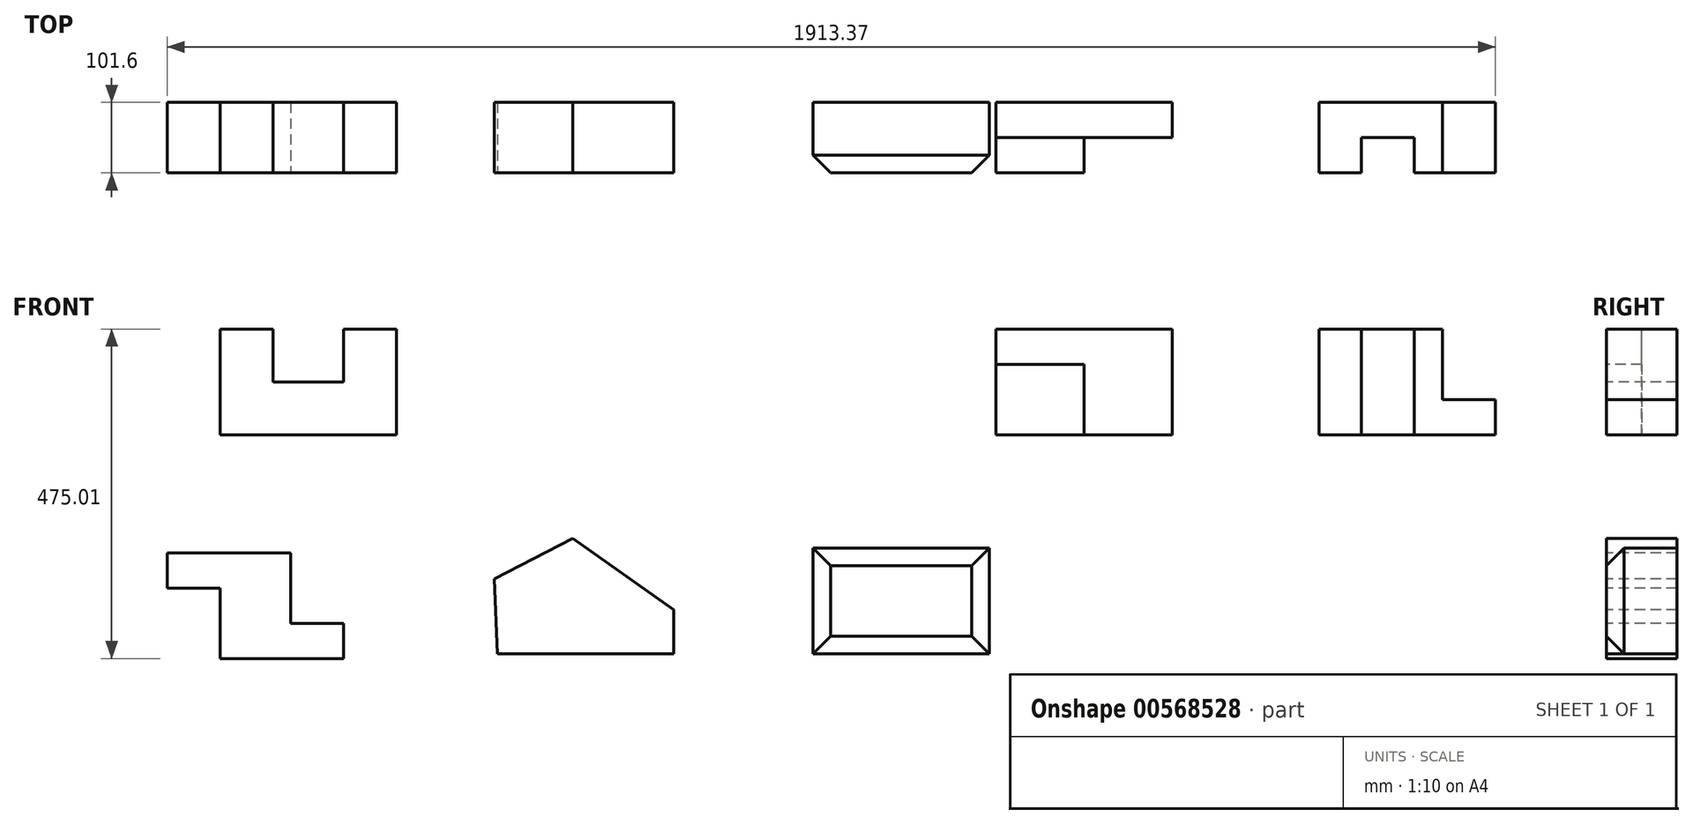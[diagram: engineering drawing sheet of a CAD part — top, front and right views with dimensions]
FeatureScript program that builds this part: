
annotation { "Feature Type Name" : "Feature", "Feature Type Description" : "" }
export const myFeature = defineFeature(function(context is Context, id is Id, definition is map)
    precondition{}
    {
        {
            var Q0;
            Q0=qCreatedBy(makeId("Front.planeOp"),FACE);
            var sketch = newSketch(context, id + "F0", { "sketchPlane" : qUnion([Q0])});
            skLineSegment(sketch, "E0", {"start": v(0, 0) * mm, "end": v(254, 0) * mm});
            skLineSegment(sketch, "E1", {"start": v(254, 0) * mm, "end": v(254, 152.4) * mm});
            skLineSegment(sketch, "E2", {"start": v(254, 152.4) * mm, "end": v(177.8, 152.4) * mm});
            skLineSegment(sketch, "E3", {"start": v(177.8, 152.4) * mm, "end": v(177.8, 76.2) * mm});
            skLineSegment(sketch, "E4", {"start": v(177.8, 76.2) * mm, "end": v(76.2, 76.2) * mm});
            skLineSegment(sketch, "E5", {"start": v(76.2, 76.2) * mm, "end": v(76.2, 152.4) * mm});
            skLineSegment(sketch, "E6", {"start": v(76.2, 152.4) * mm, "end": v(0, 152.4) * mm});
            skLineSegment(sketch, "E7", {"start": v(0, 152.4) * mm, "end": v(0, 0) * mm});
            skSolve(sketch);
        }
        {
            var Q0;
            Q0=makeQuery(id+"F0.imprint","IMPRINT",FACE,{"disambiguationData":[TD([[makeQuery(id+"F0.imprint","IMPRINT",EDGE,{"derivedFrom":sQuery(id+"F0.wireOp",EDGE,"E0")}),1.0]])]});
            extrude(context, id + "F1", {"entities" : qUnion([Q0]), "oppositeDirection" : true, "depth" : 101.6 * mm, "offsetDistance" : 25.4 * mm});
        }
        {
            var Q0;
            Q0=qCreatedBy(makeId("Front.planeOp"),FACE);
            var sketch = newSketch(context, id + "F2", { "sketchPlane" : qUnion([Q0])});
            skLineSegment(sketch, "E8.bottom", {"start": v(1117.43, 0) * mm, "end": v(1371.43, 0) * mm});
            skLineSegment(sketch, "E8.top", {"start": v(1117.43, 152.4) * mm, "end": v(1371.43, 152.4) * mm});
            skLineSegment(sketch, "E8.left", {"start": v(1117.43, 0) * mm, "end": v(1117.43, 152.4) * mm});
            skLineSegment(sketch, "E8.right", {"start": v(1371.43, 0) * mm, "end": v(1371.43, 152.4) * mm});
            skSolve(sketch);
        }
        {
            var Q0;
            Q0=makeQuery(id+"F2.imprint","IMPRINT",FACE,{"disambiguationData":[TD([[makeQuery(id+"F2.imprint","IMPRINT",EDGE,{"derivedFrom":sQuery(id+"F2.wireOp",EDGE,"E8.bottom")}),1.0]])]});
            extrude(context, id + "F3", {"entities" : qUnion([Q0]), "oppositeDirection" : true, "depth" : 101.6 * mm, "offsetDistance" : 25.4 * mm});
        }
        {
            var Q0;
            Q0=makeQuery(id+"F3.opExtrude","CAP_FACE",FACE,{"disambiguationData":[OSD([sQuery(id+"F2.wireOp",EDGE,"E8.bottom"),sQuery(id+"F2.wireOp",EDGE,"E8.top"),sQuery(id+"F2.wireOp",EDGE,"E8.left"),sQuery(id+"F2.wireOp",EDGE,"E8.right")])],"isStart":true});
            var sketch = newSketch(context, id + "F4", { "sketchPlane" : qUnion([Q0])});
            skLineSegment(sketch, "E9", {"start": v(1117.43, 76.2) * mm, "end": v(1244.43, 76.2) * mm});
            skLineSegment(sketch, "E10", {"start": v(1244.43, 0) * mm, "end": v(1371.43, 0) * mm});
            skLineSegment(sketch, "E11", {"start": v(1371.43, 0) * mm, "end": v(1371.43, 152.4) * mm});
            skLineSegment(sketch, "E12", {"start": v(1371.43, 152.4) * mm, "end": v(1117.43, 152.4) * mm});
            skLineSegment(sketch, "E13", {"start": v(1117.43, 152.4) * mm, "end": v(1117.43, 76.2) * mm});
            skLineSegment(sketch, "E14", {"start": v(1244.43, 76.2) * mm, "end": v(1244.43, 0) * mm});
            skSolve(sketch);
        }
        {
            var Q0;
            {var subQ0=sQuery(id+"F4.wireOp",EDGE,"E9");Q0=makeQuery(id+"F4.imprint","IMPRINT",FACE,{"disambiguationData":[TD([[makeQuery(id+"F4.imprint","IMPRINT",EDGE,{"derivedFrom":subQ0}),-1.0]])]});}
            extrude(context, id + "F5", {"entities" : qUnion([Q0]), "operationType" : NewBodyOperationType.ADD, "depth" : 50.8 * mm, "offsetDistance" : 25.4 * mm});
        }
        {
            var Q0;
            Q0=makeQuery(id+"F5.opExtrude","CAP_FACE",FACE,{"disambiguationData":[OSD([sQuery(id+"F2.wireOp",EDGE,"E8.bottom"),sQuery(id+"F2.wireOp",EDGE,"E8.left"),sQuery(id+"F4.wireOp",EDGE,"E9"),sQuery(id+"F4.wireOp",EDGE,"E14")])],"isStart":false});
            extrude(context, id + "F6", {"entities" : qUnion([Q0]), "operationType" : NewBodyOperationType.ADD, "oppositeDirection" : true, "depth" : 50.8 * mm, "offsetDistance" : 25.4 * mm});
        }
        {
            var Q0;
            Q0=makeQuery(id+"F5.opExtrude","CAP_FACE",FACE,{"disambiguationData":[OSD([sQuery(id+"F2.wireOp",EDGE,"E8.bottom"),sQuery(id+"F2.wireOp",EDGE,"E8.left"),sQuery(id+"F4.wireOp",EDGE,"E9"),sQuery(id+"F4.wireOp",EDGE,"E14")])],"isStart":false});
            extrude(context, id + "F7", {"entities" : qUnion([Q0]), "operationType" : NewBodyOperationType.ADD, "oppositeDirection" : true, "depth" : 50.8 * mm, "offsetDistance" : 25.4 * mm});
        }
        {
            var Q0;
            Q0=makeQuery(id+"F5.opExtrude","CAP_FACE",FACE,{"disambiguationData":[OSD([sQuery(id+"F2.wireOp",EDGE,"E8.bottom"),sQuery(id+"F2.wireOp",EDGE,"E8.left"),sQuery(id+"F4.wireOp",EDGE,"E9"),sQuery(id+"F4.wireOp",EDGE,"E14")])],"isStart":false});
            extrude(context, id + "F8", {"entities" : qUnion([Q0]), "operationType" : NewBodyOperationType.REMOVE, "oppositeDirection" : true, "depth" : 50.8 * mm, "offsetDistance" : 25.4 * mm});
        }
        {
            var Q0;
            {var subQ0=sQuery(id+"F2.wireOp",EDGE,"E8.left");var subQ1=sQuery(id+"F2.wireOp",EDGE,"E8.bottom");Q0=makeQuery(id+"F8.boolean.opBoolean","MERGE",FACE,{"derivedFrom":[makeQuery(id+"F3.opExtrude","CAP_FACE",FACE,{"disambiguationData":[OSD([subQ1,sQuery(id+"F2.wireOp",EDGE,"E8.top"),subQ0,sQuery(id+"F2.wireOp",EDGE,"E8.right")])],"isStart":true}),makeQuery(id+"F8.opExtrude","CAP_FACE",FACE,{"disambiguationData":[OSD([subQ1,subQ0,sQuery(id+"F4.wireOp",EDGE,"E9"),sQuery(id+"F4.wireOp",EDGE,"E14")])],"isStart":false})]});}
            var sketch = newSketch(context, id + "F9", { "sketchPlane" : qUnion([Q0])});
            skLineSegment(sketch, "E15", {"start": v(1117.43, 76.2) * mm, "end": v(1244.43, 76.2) * mm});
            skLineSegment(sketch, "E16", {"start": v(1244.43, 76.2) * mm, "end": v(1244.43, 0) * mm});
            skPoint(sketch, "E16.endSnap0", {"position": v(1244.43, 0) * mm});
            skLineSegment(sketch, "E17", {"start": v(1244.43, 0) * mm, "end": v(1371.43, 0) * mm});
            skLineSegment(sketch, "E18", {"start": v(1371.43, 0) * mm, "end": v(1371.43, 152.4) * mm});
            skLineSegment(sketch, "E19", {"start": v(1371.43, 152.4) * mm, "end": v(1117.43, 152.4) * mm});
            skLineSegment(sketch, "E20", {"start": v(1117.43, 152.4) * mm, "end": v(1117.43, 76.2) * mm});
            skSolve(sketch);
        }
        {
            var Q0;
            Q0=makeQuery(id+"F9.imprint","IMPRINT",FACE,{"disambiguationData":[TD([[makeQuery(id+"F9.imprint","IMPRINT",EDGE,{"derivedFrom":sQuery(id+"F9.wireOp",EDGE,"E15")}),1.0]])]});
            extrude(context, id + "F10", {"entities" : qUnion([Q0]), "operationType" : NewBodyOperationType.REMOVE, "oppositeDirection" : true, "depth" : 50.8 * mm, "offsetDistance" : 25.4 * mm});
        }
        {
            var Q0;
            Q0=makeQuery(id+"F10.boolean.opBoolean","COPY",FACE,{"derivedFrom":makeQuery(id+"F10.opExtrude","SWEPT_FACE",FACE,{"disambiguationData":[OSD([sQuery(id+"F9.wireOp",EDGE,"E15")])]})});
            extrude(context, id + "F11", {"entities" : qUnion([Q0]), "operationType" : NewBodyOperationType.ADD, "depth" : 25.4 * mm, "offsetDistance" : 25.4 * mm});
        }
        {
            var Q0;
            Q0=qCreatedBy(makeId("Front.planeOp"),FACE);
            var sketch = newSketch(context, id + "F12", { "sketchPlane" : qUnion([Q0])});
            skLineSegment(sketch, "E21", {"start": v(1633.97, 152.4) * mm, "end": v(1583.17, 152.4) * mm});
            skLineSegment(sketch, "E22", {"start": v(1583.17, 152.4) * mm, "end": v(1583.17, 0) * mm});
            skLineSegment(sketch, "E23", {"start": v(1583.17, 0) * mm, "end": v(1633.97, 0) * mm});
            skLineSegment(sketch, "E24", {"start": v(1633.97, 0) * mm, "end": v(1633.97, 152.4) * mm});
            skLineSegment(sketch, "E25", {"start": v(1633.97, 152.4) * mm, "end": v(1760.97, 152.4) * mm});
            skLineSegment(sketch, "E26", {"start": v(1760.97, 152.4) * mm, "end": v(1760.97, 50.8) * mm});
            skLineSegment(sketch, "E27", {"start": v(1760.97, 50.8) * mm, "end": v(1837.17, 50.8) * mm});
            skLineSegment(sketch, "E28", {"start": v(1837.17, 50.8) * mm, "end": v(1837.17, 0) * mm});
            skLineSegment(sketch, "E29", {"start": v(1837.17, 0) * mm, "end": v(1633.97, 0) * mm});
            skSolve(sketch);
        }
        {
            var Q0;
            Q0=makeQuery(id+"F12.imprint","IMPRINT",FACE,{"disambiguationData":[TD([[makeQuery(id+"F12.imprint","IMPRINT",EDGE,{"derivedFrom":sQuery(id+"F12.wireOp",EDGE,"E24")}),-1.0]])]});
            var Q1;
            Q1=makeQuery(id+"F12.imprint","IMPRINT",FACE,{"disambiguationData":[TD([[makeQuery(id+"F12.imprint","IMPRINT",EDGE,{"derivedFrom":sQuery(id+"F12.wireOp",EDGE,"E21")}),1.0]])]});
            extrude(context, id + "F13", {"entities" : qUnion([Q0, Q1]), "oppositeDirection" : true, "depth" : 50.8 * mm, "offsetDistance" : 25.4 * mm});
        }
        {
            var Q0;
            Q0=makeQuery(id+"F13.opExtrude","CAP_FACE",FACE,{"disambiguationData":[OSD([sQuery(id+"F12.wireOp",EDGE,"E21"),sQuery(id+"F12.wireOp",EDGE,"E22"),sQuery(id+"F12.wireOp",EDGE,"E23"),sQuery(id+"F12.wireOp",EDGE,"E25"),sQuery(id+"F12.wireOp",EDGE,"E26"),sQuery(id+"F12.wireOp",EDGE,"E27"),sQuery(id+"F12.wireOp",EDGE,"E28"),sQuery(id+"F12.wireOp",EDGE,"E29")])],"isStart":true});
            extrude(context, id + "F14", {"entities" : qUnion([Q0]), "operationType" : NewBodyOperationType.ADD, "oppositeDirection" : true, "depth" : 101.6 * mm, "offsetDistance" : 25.4 * mm});
        }
        {
            var Q0;
            {var subQ0=sQuery(id+"F12.wireOp",EDGE,"E25");var subQ1=sQuery(id+"F12.wireOp",EDGE,"E21");Q0=makeQuery(id+"F14.boolean.opBoolean","MERGE",FACE,{"derivedFrom":[makeQuery(id+"F13.opExtrude","SWEPT_FACE",FACE,{"disambiguationData":[OSD([subQ1,subQ0])]}),makeQuery(id+"F14.opExtrude","SWEPT_FACE",FACE,{"disambiguationData":[OSD([subQ1,subQ0])]})]});}
            var sketch = newSketch(context, id + "F15", { "sketchPlane" : qUnion([Q0])});
            skLineSegment(sketch, "E30", {"start": v(1644.38, 0) * mm, "end": v(1644.38, 50.8) * mm});
            skLineSegment(sketch, "E31", {"start": v(1644.38, 50.8) * mm, "end": v(1720.58, 50.8) * mm});
            skLineSegment(sketch, "E32", {"start": v(1720.58, 50.8) * mm, "end": v(1720.58, 0) * mm});
            skSolve(sketch);
        }
        {
            var Q0;
            {var subQ0=sQuery(id+"F15.wireOp",EDGE,"E30");Q0=makeQuery(id+"F15.imprint","IMPRINT",FACE,{"disambiguationData":[TD([[makeQuery(id+"F15.imprint","IMPRINT",EDGE,{"derivedFrom":subQ0}),-1.0]])]});}
            extrude(context, id + "F16", {"entities" : qUnion([Q0]), "operationType" : NewBodyOperationType.REMOVE, "oppositeDirection" : true, "depth" : 152.4 * mm, "offsetDistance" : 25.4 * mm});
        }
        {
            var Q0;
            Q0=qCreatedBy(makeId("Front.planeOp"),FACE);
            var sketch = newSketch(context, id + "F17", { "sketchPlane" : qUnion([Q0])});
            skLineSegment(sketch, "E33", {"start": v(0, -322.6) * mm, "end": v(177.8, -322.6) * mm});
            skLineSegment(sketch, "E34", {"start": v(177.8, -322.6) * mm, "end": v(177.8, -271.8) * mm});
            skLineSegment(sketch, "E35", {"start": v(177.8, -271.8) * mm, "end": v(101.6, -271.8) * mm});
            skLineSegment(sketch, "E36", {"start": v(101.6, -271.8) * mm, "end": v(101.6, -170.2) * mm});
            skLineSegment(sketch, "E37", {"start": v(101.6, -170.2) * mm, "end": v(-76.2, -170.2) * mm});
            skLineSegment(sketch, "E38", {"start": v(-76.2, -170.2) * mm, "end": v(-76.2, -221) * mm});
            skLineSegment(sketch, "E39", {"start": v(-76.2, -221) * mm, "end": v(0, -221) * mm});
            skLineSegment(sketch, "E40", {"start": v(0, -221) * mm, "end": v(0, -322.6) * mm});
            skSolve(sketch);
        }
        {
            var Q0;
            Q0=makeQuery(id+"F17.imprint","IMPRINT",FACE,{"disambiguationData":[TD([[makeQuery(id+"F17.imprint","IMPRINT",EDGE,{"derivedFrom":sQuery(id+"F17.wireOp",EDGE,"E33")}),1.0]])]});
            extrude(context, id + "F18", {"entities" : qUnion([Q0]), "oppositeDirection" : true, "depth" : 101.6 * mm, "offsetDistance" : 25.4 * mm});
        }
        {
            var Q0;
            Q0=qCreatedBy(makeId("Front.planeOp"),FACE);
            var sketch = newSketch(context, id + "F19", { "sketchPlane" : qUnion([Q0])});
            skLineSegment(sketch, "E41", {"start": v(399.36, -315.5) * mm, "end": v(653.36, -315.5) * mm});
            skLineSegment(sketch, "E42", {"start": v(653.36, -315.5) * mm, "end": v(653.36, -252) * mm});
            skLineSegment(sketch, "E43", {"start": v(653.36, -252) * mm, "end": v(508.06, -149.52) * mm});
            skLineSegment(sketch, "E44", {"start": v(508.06, -149.52) * mm, "end": v(395.13, -207.62) * mm});
            skLineSegment(sketch, "E45", {"start": v(395.13, -207.62) * mm, "end": v(399.36, -315.5) * mm});
            skSolve(sketch);
        }
        {
            var Q0;
            Q0=makeQuery(id+"F19.imprint","IMPRINT",FACE,{"disambiguationData":[TD([[makeQuery(id+"F19.imprint","IMPRINT",EDGE,{"derivedFrom":sQuery(id+"F19.wireOp",EDGE,"E41")}),1.0]])]});
            extrude(context, id + "F20", {"entities" : qUnion([Q0]), "oppositeDirection" : true, "depth" : 101.6 * mm, "offsetDistance" : 25.4 * mm});
        }
        {
            var Q0;
            Q0=qCreatedBy(makeId("Front.planeOp"),FACE);
            var sketch = newSketch(context, id + "F21", { "sketchPlane" : qUnion([Q0])});
            skLineSegment(sketch, "E46", {"start": v(854.24, -315.55) * mm, "end": v(1108.24, -315.55) * mm});
            skLineSegment(sketch, "E47", {"start": v(1108.24, -315.55) * mm, "end": v(1108.24, -163.15) * mm});
            skLineSegment(sketch, "E48", {"start": v(1108.24, -163.15) * mm, "end": v(854.24, -163.15) * mm});
            skLineSegment(sketch, "E49", {"start": v(854.24, -163.15) * mm, "end": v(854.24, -315.55) * mm});
            skSolve(sketch);
        }
        {
            var Q0;
            Q0=makeQuery(id+"F21.imprint","IMPRINT",FACE,{"disambiguationData":[TD([[makeQuery(id+"F21.imprint","IMPRINT",EDGE,{"derivedFrom":sQuery(id+"F21.wireOp",EDGE,"E46")}),1.0]])]});
            extrude(context, id + "F22", {"entities" : qUnion([Q0]), "oppositeDirection" : true, "depth" : 101.6 * mm, "offsetDistance" : 25.4 * mm});
        }
        {
            var Q0;
            Q0=makeQuery(id+"F22.opExtrude","CAP_FACE",FACE,{"disambiguationData":[OSD([sQuery(id+"F21.wireOp",EDGE,"E46"),sQuery(id+"F21.wireOp",EDGE,"E47"),sQuery(id+"F21.wireOp",EDGE,"E48"),sQuery(id+"F21.wireOp",EDGE,"E49")])],"isStart":true});
            chamfer(context, id + "F23", {"entities" : qUnion([Q0]), "width" : 25.4 * mm, "tangentPropagation" : true});
        }
    });
